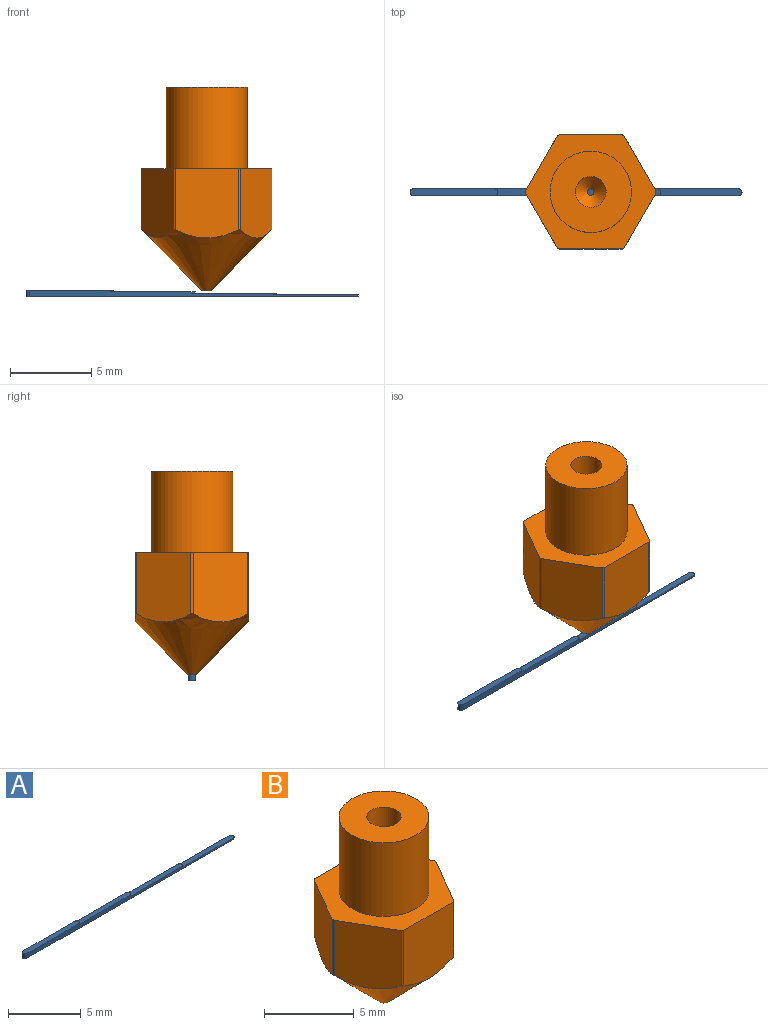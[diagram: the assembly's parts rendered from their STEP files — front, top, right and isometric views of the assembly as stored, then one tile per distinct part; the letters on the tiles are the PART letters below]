
ASSEMBLY  parts=2 mates=2
PART A: 12 faces, bbox 20.4x0.4x0.4 mm
  f0: plane 20x0.4mm, normal (0,1,0), area 5mm2, adj f1,f3,f4,f5,f6,f7,f8,f9
  f1: cylinder r=0.2mm len=0.4mm, axis (0,0,-1), area 0.3mm2, adj f0,f2,f5,f11
  f2: plane 20x0.4mm, normal (0,-1,0), area 5mm2, adj f1,f3,f4,f5,f6,f7,f8,f9
  f3: cylinder r=0.2mm len=0.4mm, axis (0,0,-1), area 0.1mm2, adj f0,f2,f4,f5
  f4: plane 5.2x0.4mm, normal (0,0,1), area 2mm2, adj f0,f2,f3,f6
  f5: plane 20.4x0.4mm, normal (0,0,-1), area 8.1mm2, adj f0,f1,f2,f3
  f6: cylinder r=0.2mm len=0.4mm, axis (0,0,-1), area 0.1mm2, adj f0,f2,f4,f7
  f7: plane 5.2x0.4mm, normal (0,0,1), area 2mm2, adj f0,f2,f6,f8
  f8: cylinder r=0.2mm len=0.4mm, axis (0,0,-1), area 0.1mm2, adj f0,f2,f7,f9
  f9: plane 5.2x0.4mm, normal (0,0,1), area 2mm2, adj f0,f2,f8,f10
  f10: cylinder r=0.2mm len=0.4mm, axis (0,0,-1), area 0.1mm2, adj f0,f2,f9,f11
  f11: plane 5.4x0.4mm, normal (0,0,1), area 2.1mm2, adj f0,f1,f2,f10
PART B: 20 faces, bbox 8x8x12.5 mm
  f0: cylinder r=4mm len=3.75mm, axis (0,0,-1), area 0.5mm2, adj f6,f7,f18,f19
  f1: cylinder r=4mm len=3.75mm, axis (0,0,-1), area 0.5mm2, adj f6,f7,f14,f19
  f2: cylinder r=4mm len=3.75mm, axis (0,0,-1), area 0.5mm2, adj f6,f7,f17,f18
  f3: cylinder r=4mm len=3.75mm, axis (0,0,-1), area 0.5mm2, adj f6,f7,f16,f17
  f4: cylinder r=4mm len=3.75mm, axis (0,0,-1), area 0.5mm2, adj f6,f7,f15,f16
  f5: cylinder r=4mm len=3.75mm, axis (0,0,-1), area 0.5mm2, adj f6,f7,f14,f15
  f6: cone r=4mm half-angle=45deg, axis (0,0,1), area 59.6mm2, adj f0,f1,f2,f3,f4,f5,f8,f14
  f7: plane 8x7mm, normal (0,0,1), area 22.8mm2, adj f0,f1,f2,f3,f4,f5,f13,f14
  f8: plane 0.6x0.6mm, normal (0,0,-1), area 0.2mm2, adj f6,f9
  f9: cylinder r=0.2mm len=0.7mm, axis (0,0,-1), area 0.9mm2, adj f8,f10
  f10: cone r=0.2mm half-angle=45deg, axis (0,0,1), area 3.8mm2, adj f9,f11
  f11: cylinder r=0.95mm len=11mm, axis (0,0,-1), area 65.7mm2, adj f10,f12
  f12: plane 5x5mm, normal (0,0,1), area 16.8mm2, adj f11,f13
  f13: cylinder r=2.5mm len=5mm, axis (0,0,-1), area 78.5mm2, adj f7,f12
  f14: plane 4.26x3.36mm, normal (-0.87,0.5,0), area 15.8mm2, adj f1,f5,f6,f7
  f15: plane 4.26x3.36mm, normal (-0.87,-0.5,0), area 15.8mm2, adj f4,f5,f6,f7
  f16: plane 4.26x3.88mm, normal (0,-1,0), area 15.8mm2, adj f3,f4,f6,f7
  f17: plane 4.26x3.36mm, normal (0.87,-0.5,0), area 15.8mm2, adj f2,f3,f6,f7
  f18: plane 4.26x3.36mm, normal (0.87,0.5,0), area 15.8mm2, adj f0,f2,f6,f7
  f19: plane 4.26x3.88mm, normal (0,1,0), area 15.8mm2, adj f0,f1,f6,f7
PLACE A t=(0,0,-0.4)mm
PLACE B t=(10.9,0,0)mm
MATE pin_slot B.f0 <-> A.f8  axis (0,0,1) through (10.9,0,0)mm
MATE parallel B.f16 <-> A.f2  axis (0,-1,0) through (10.9,-3.5,5.41)mm
